# Revit family: Furniture_Storage_Spacestor_Andante Credenza
name_source: partatom
category: Furniture
revit_build: Autodesk Revit 2015 (Build: 20140223_1515(x64)
units: mm (PartAtom-declared; Revit-internal decimal feet)

## types (3) — shared parameters
Back Width = 340 mm  [stored 1.11549 ft]
Leg Number = 2
Spacestor_Andante Credenza_Casework = Spacestor White Table Top
Spacestor_Andante Credenza_Framework = Spacestor Polished Steel
Spacestor_Andante Credenza_Handle = Spacestor Polished Steel

## per-type parameters (varying)
| type | Door Number | Width |
| 2-door - 854w x 600d x 900h | 1 | 854 mm  [stored 2.80184 ft] |
| 4-door - 1654w x 600d x 900h | 2 | 1654 mm  [stored 5.42651 ft] |
| 6-door - 2454w x 600d x 900h | 3 | 2454 mm  [stored 8.05118 ft] |

note: [stored X ft] marks values corroborated as IEEE doubles in the binary element streams (Revit-internal decimal feet)

## geometry (parser evidence)
native form markers: Blend x2, Sweep x18
no freeform markers — native parametric forms only
